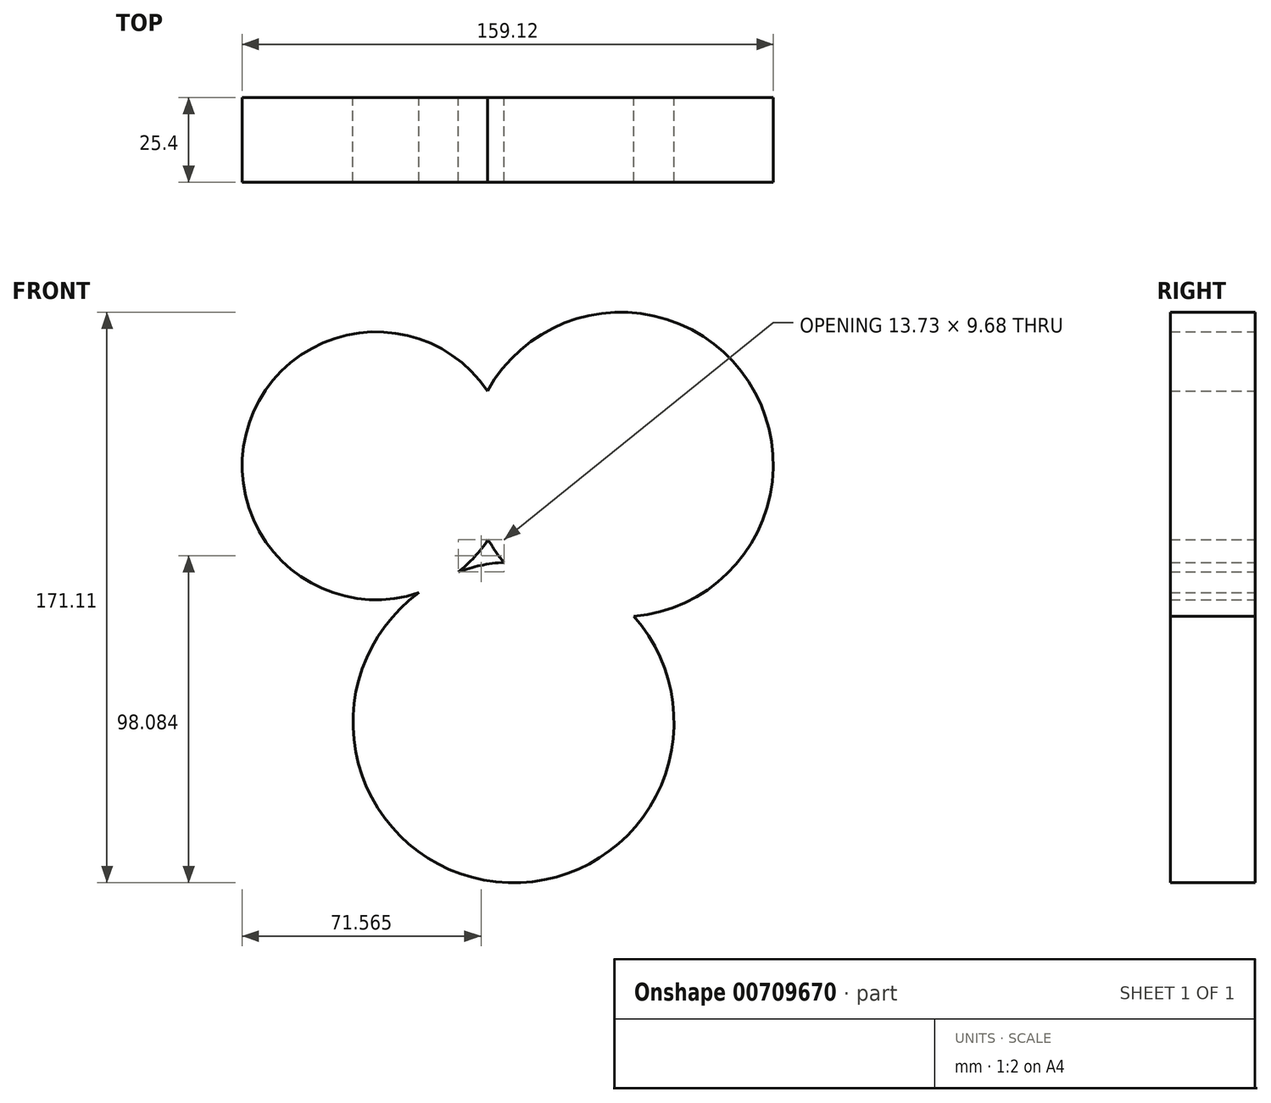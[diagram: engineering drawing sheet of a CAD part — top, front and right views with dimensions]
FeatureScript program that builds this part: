
annotation { "Feature Type Name" : "Feature", "Feature Type Description" : "" }
export const myFeature = defineFeature(function(context is Context, id is Id, definition is map)
    precondition{}
    {
        {
            var Q0;
            Q0=qCreatedBy(makeId("Front.planeOp"),FACE);
            var sketch = newSketch(context, id + "F0", { "sketchPlane" : qUnion([Q0])});
            skCircle(sketch, "E0", {"center": v(-41.12, 40.93) * mm, "radius": 40.18 * mm});
            skCircle(sketch, "E1", {"center": v(32.15, 41.3) * mm, "radius": 45.68 * mm});
            skCircle(sketch, "E2", {"center": v(0, -36.04) * mm, "radius": 48.1 * mm});
            skSolve(sketch);
        }
        {
            var Q0;
            Q0 = qSketchRegion(id + "F0", true);
            extrude(context, id + "F1", {"entities" : qUnion([Q0]), "depth" : 25.4 * mm, "offsetDistance" : 25.4 * mm});
        }
    });
